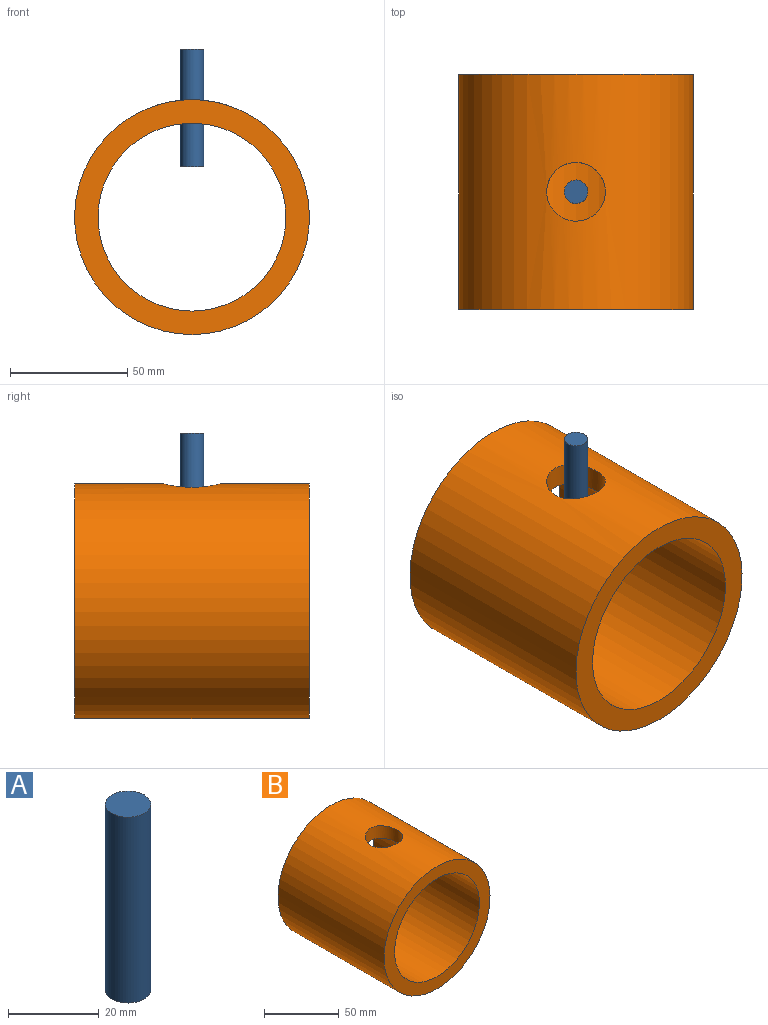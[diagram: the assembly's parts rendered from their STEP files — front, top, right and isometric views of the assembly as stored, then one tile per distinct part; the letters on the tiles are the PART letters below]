
ASSEMBLY  parts=2 mates=1
PART A: 3 faces, bbox 10x10x50 mm
  f0: cylinder r=5mm len=50mm, axis (0,0,-1), area 1570.8mm2, adj f1,f2
  f1: plane 10x10mm, normal (0,0,1), area 78.5mm2, adj f0
  f2: plane 10x10mm, normal (0,0,-1), area 78.5mm2, adj f0
PART B: 5 faces, bbox 100x100x100 mm
  f0: cylinder r=40mm len=100mm, axis (0,-1,0), area 24636.8mm2, adj f2,f3,f4
  f1: cylinder r=50mm len=100mm, axis (0,-1,0), area 30921.9mm2, adj f2,f3,f4
  f2: plane 100x100mm, normal (0,1,0), area 2827.4mm2, adj f0,f1
  f3: plane 100x100mm, normal (0,-1,0), area 2827.4mm2, adj f0,f1
  f4: cylinder r=12.5mm len=25mm, axis (0,0,-1), area 801.5mm2, adj f0,f1
PLACE A rot(axis=(0,0,1),11.4deg) t=(-18.66,2.03,40.61)mm
PLACE B t=(-18.66,-47.97,19.2)mm fixed
MATE cylindrical A.f0 <-> B.f4  axis (0,0,-1) through (-18.66,2.03,90.61)mm
